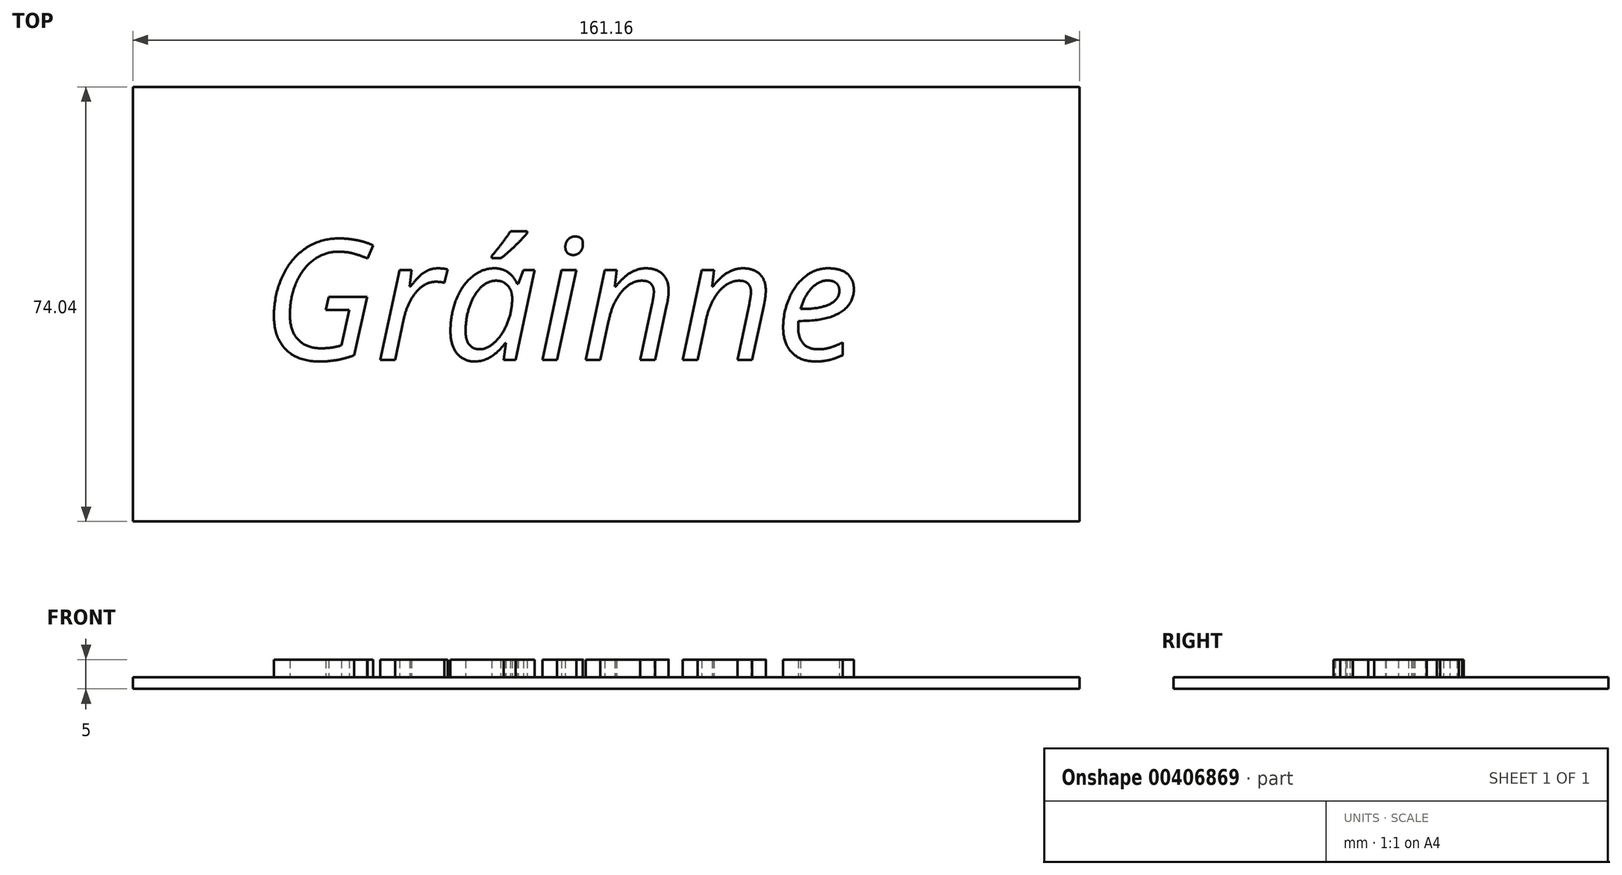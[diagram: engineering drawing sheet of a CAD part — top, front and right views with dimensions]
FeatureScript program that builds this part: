
annotation { "Feature Type Name" : "Feature", "Feature Type Description" : "" }
export const myFeature = defineFeature(function(context is Context, id is Id, definition is map)
    precondition{}
    {
        {
            var Q0;
            Q0=qCreatedBy(makeId("Top.planeOp"),FACE);
            var sketch = newSketch(context, id + "F0", { "sketchPlane" : qUnion([Q0])});
            skLineSegment(sketch, "E0.bottom", {"start": v(-124.56, 46.5) * mm, "end": v(36.6, 46.5) * mm});
            skLineSegment(sketch, "E0.top", {"start": v(-124.56, -27.54) * mm, "end": v(36.6, -27.54) * mm});
            skLineSegment(sketch, "E0.left", {"start": v(-124.56, 46.5) * mm, "end": v(-124.56, -27.54) * mm});
            skLineSegment(sketch, "E0.right", {"start": v(36.6, 46.5) * mm, "end": v(36.6, -27.54) * mm});
            skSolve(sketch);
        }
        {
            var Q0;
            Q0 = qSketchRegion(id + "F0", true);
            extrude(context, id + "F1", {"entities" : qUnion([Q0]), "depth" : 2 * mm});
        }
        {
            var Q0;
            Q0=makeQuery(id+"F1.opExtrude","CAP_FACE",FACE,{"disambiguationData":[OSD([sQuery(id+"F0.wireOp",EDGE,"E0.bottom"),sQuery(id+"F0.wireOp",EDGE,"E0.top"),sQuery(id+"F0.wireOp",EDGE,"E0.left"),sQuery(id+"F0.wireOp",EDGE,"E0.right")])],"isStart":false});
            var sketch = newSketch(context, id + "F2", { "sketchPlane" : qUnion([Q0])});
            skText(sketch, "E1", { "text": "Gráinne", "fontName": "NotoSans-Italic.ttf"});
            const initialGuessF2  = {"E1": [-0.10262, 0, 1, 0, 0.02056]};
            skSetInitialGuess(sketch, initialGuessF2);
            skSolve(sketch);
        }
        {
            var Q0;
            Q0 = qSketchRegion(id + "F2", true);
            extrude(context, id + "F3", {"entities" : qUnion([Q0]), "operationType" : NewBodyOperationType.ADD, "depth" : 3 * mm});
        }
    });
